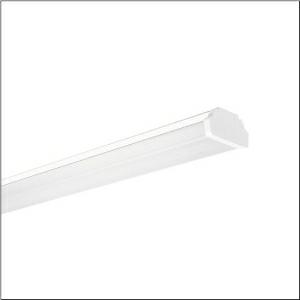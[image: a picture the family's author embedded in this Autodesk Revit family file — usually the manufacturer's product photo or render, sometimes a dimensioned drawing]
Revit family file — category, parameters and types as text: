
# Revit family: dus_r__31_gen_2_53bd812cv4dxd2_dd4f
name_source: partatom
category: Lighting Fixtures
units: mm (PartAtom-declared; Revit-internal decimal feet)

## family parameters
Cut with Voids When Loaded = No
Host = Face
Light Source = No
Part Type = Normal
Room Calculation Point = No
Round Connector Dimension = Use Diameter
Shared = No

## types (1)
- --- (1 x LED, 13040 lm, 68.5 W, 4000K)
    Apparent Load = 69 VA
    CIE Flux Codes = 47 80 95 93 100
    Color Rendering = 80
    Color Temperature = 4000K
    Default Elevation = 1800 mm
    Description = DUS® 31 Gen.2, luminaire insert, of sheet steel, coil coated, white, length: 1.535mm, width: 81mm, height: 90mm, 5x system unit, system units: 307mm, LED rated luminous flux: 13.040lm, light colour: 840, control gear: ON/OFF Multilumen, CLOi, with plug, 3-pole, with phase selection, mains connection: 220..240V, AC, 50/60Hz, start of lifetime: 69W, end of service life: 82W, through-wiring accessed according to module size, primary optical cover: cover, of PMMA, light emission: direct distribution, primary light characteristic: symmetric, protection rating (complete): IP20, protection rating (LED compartment): IP50, insulation class (complete): insulation class I (protective earthing), certification: CE, ENEC, VDE, UKCA, impact resistance: IK03, permissible ambient temperature for indoor applications: -35..+35°C, corresponds to IFS (International Featured Standards) requirements for safety and quality in the food industry, reducing of maximum allowable ambient temperature of 5°C with ceiling mounting, packaging unit: 1 piece
    Height = 95 mm
    Lamp = 1 x LED
    Lamp Light Flux = 13040 lm
    Lamp Power = 68.5 W
    Lamp count = 1
    Length = 1535 mm
    Luminous efficacy = 190 lm/W
    Manufacturer = Siteco
    ModVariant = No
    Model = 53BD812CV4DXD2
    Mounting Place = Ceiling
    Mounting Type = Pendant
    Number of Poles = 1
    OnlyDefault = Yes
    Power Factor = 1
    Product Name = DUS® 31 Gen.2
    Product group = luminaire insert | ceiling pendant
    ProductGroupID = 902
    Protection Class = Protection class I
    Protection Degree = IP 20
    RLX_Detail_Level = 1
    RLX_Emergency_Light_Flux = 0 lm
    RLX_Emergency_Type = 0
    RLX_Emergency_Type_DB = No
    RlxData = <blob elided: 29893 chars, md5=938d2f99>
    Socket = socket
    Standby Power = 0 W
    System Light Flux = 13040 lm
    System Power = 69 W
    Type Comments = factory setting: luminous flux: 100 % | (A | C | E) | 161 mA
    Type Image = l_1319596.jpg
    URL = http://relux.com
    VarID = @adj_063057
    Voltage = 0 V
    Weight = 0.00 kg
    Width = 81 mm

## geometry (parser evidence)
native form markers: Blend x4, Sweep x11
no freeform markers — native parametric forms only
